FCSTD DOCUMENT  (FreeCAD 0.19R24366 (Git))
Label: 1U_v0
License: All rights reserved
LicenseURL: http://en.wikipedia.org/wiki/All_rights_reserved
objects: PartDesign::Body×2, Sketcher::SketchObject×1
note: 3 computed .brp shape members not serialized (recipe doc carries the construction recipe); baked Part::Feature solids carry a one-line shape summary decoded from their .brp

FEATURE [PartDesign::Body] Body
  Origin = -> Origin
FEATURE [Sketcher::SketchObject] Sketch
  FullyConstrained = true
  MapMode = 5
  Support = -> [XY_Plane001]
  sketch-geometry (8):
    g0: LineSegment StartX=-101.6 StartY=22.225 StartZ=0 EndX=101.6 EndY=22.225 EndZ=0
    g1: LineSegment StartX=101.6 StartY=22.225 StartZ=0 EndX=101.6 EndY=-22.225 EndZ=0
    g2: LineSegment StartX=101.6 StartY=-22.225 StartZ=0 EndX=-101.6 EndY=-22.225 EndZ=0
    g3: LineSegment StartX=-101.6 StartY=-22.225 StartZ=0 EndX=-101.6 EndY=22.225 EndZ=0
    g4: Circle CenterX=-93.6625 CenterY=15.875 CenterZ=0 NormalX=0 NormalY=0 NormalZ=1 AngleXU=0 Radius=2.775
    g5: Circle CenterX=-93.6625 CenterY=-15.875 CenterZ=0 NormalX=0 NormalY=0 NormalZ=1 AngleXU=0 Radius=2.775
    g6: Circle CenterX=93.6625 CenterY=15.875 CenterZ=0 NormalX=0 NormalY=0 NormalZ=1 AngleXU=0 Radius=2.775
    g7: Circle CenterX=93.6625 CenterY=-15.875 CenterZ=0 NormalX=0 NormalY=0 NormalZ=1 AngleXU=0 Radius=2.775
  constraints (20):
    c: Coincident(g0,g1)
    c: Coincident(g1,g2)
    c: Coincident(g2,g3)
    c: Coincident(g3,g0)
    c: Horizontal(g0)
    c: Horizontal(g2)
    c: Vertical(g1)
    c: Vertical(g3)
    c: DistanceX(g0,g0) = 203.2
    c: DistanceY(g3,g3) = 44.45
    c: Symmetric(g0,g2,g-1)
    c: Diameter(g4) = 5.55
    c: DistanceX(g0,g4) = 7.9375
    c: DistanceY(g4,g0) = 6.35
    c: Diameter(g5) = 5.55
    c: Symmetric(g4,g5,g-1)
    c: Diameter(g6) = 5.55
    c: Diameter(g7) = 5.55
    c: Symmetric(g6,g4,g-2)
    c: Symmetric(g7,g5,g-2)
FEATURE [PartDesign::Body] Body001
  Group = -> [Sketch]
  Origin = -> Origin001
